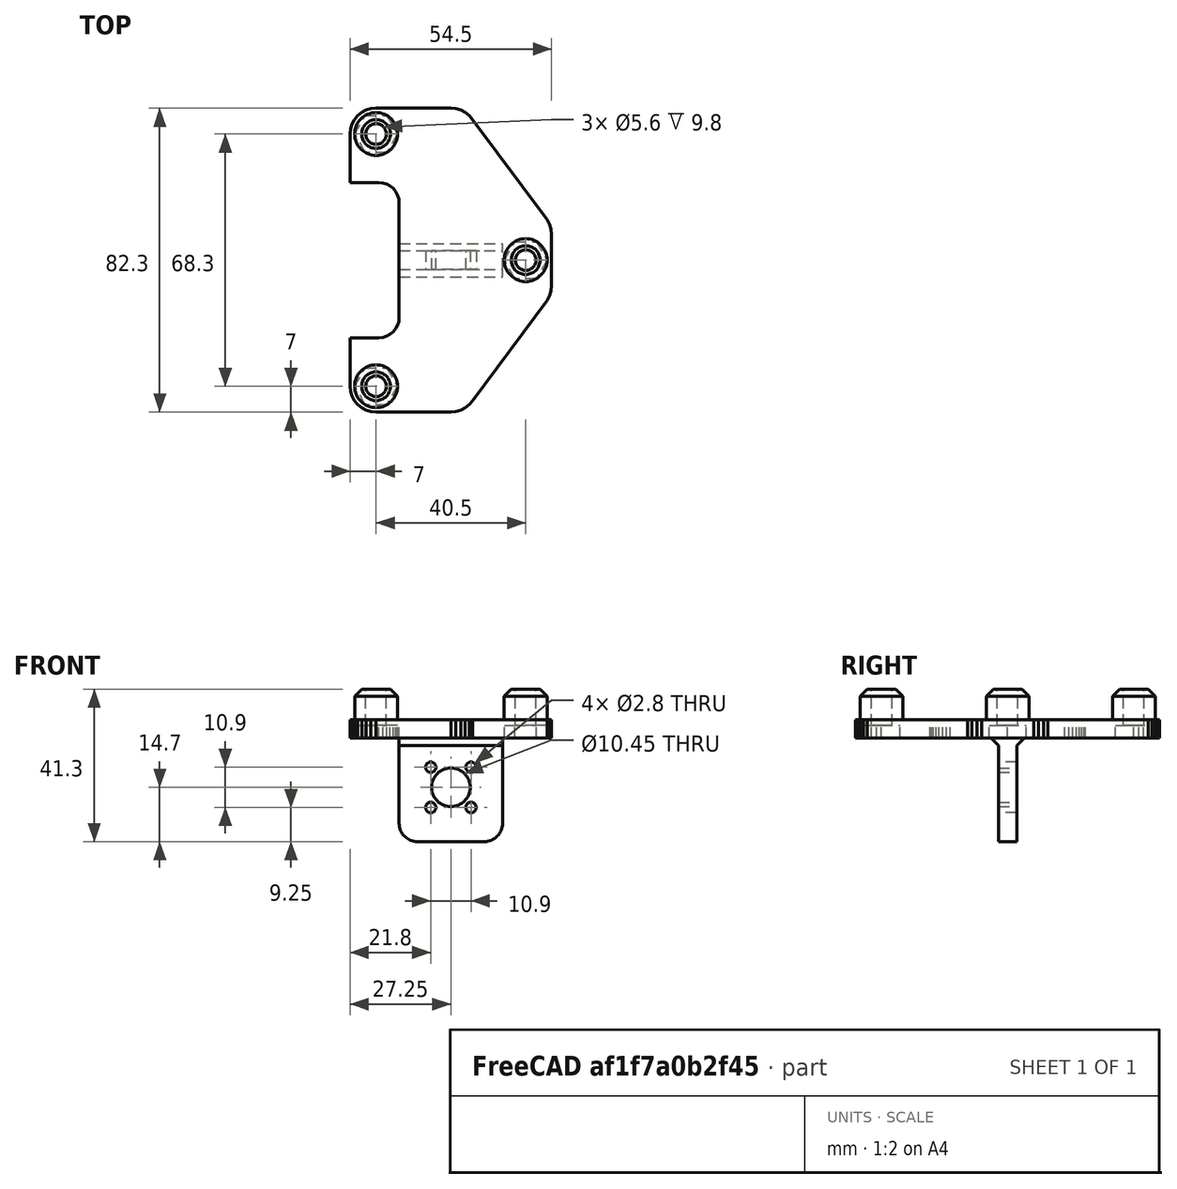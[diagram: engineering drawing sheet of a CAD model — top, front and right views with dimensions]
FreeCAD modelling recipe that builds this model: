
FCSTD DOCUMENT  (FreeCAD 0.19R24267 +99 (Git))
Label: carroZ_1
License: All rights reserved
LicenseURL: http://en.wikipedia.org/wiki/All_rights_reserved
objects: Part::Feature×75, Part::Part2DObjectPython×10, Part::Cylinder×6, Part::Cut×5, Part::FeaturePython×4, Part::MultiFuse×4, Part::Prism×4, Part::Chamfer×3, Part::Extrusion×2, Part::Fuse×2, Part::Plane×1, Part::Box×1, App::DocumentObjectGroupPython×1, Part::Refine×1, Part::Fillet×1
note: 119 computed .brp shape members not serialized (recipe doc carries the construction recipe); baked Part::Feature solids carry a one-line shape summary decoded from their .brp

FEATURE [Part::Feature] polygon
  shape: bbox 40.5 x 68.3 x 2e-07 mm, 1 faces, 0 solids (baked)
FEATURE [Part::Part2DObjectPython] circle  # Draft 2D object (typed FeaturePython)
  Area = 153.938
  FirstAngle = 0
  LastAngle = 0
  MakeFace = true
  Radius = 7
FEATURE [Part::FeaturePython] minkowski  # WARN: FeaturePython — macro-defined, semantics opaque (R4)
  Arguments = {'convexity': '0'}
  Children = -> [polygon,circle]
  Operation = minkowski
FEATURE [Part::Part2DObjectPython] circle001  # Draft 2D object (typed FeaturePython)
  Area = 24.6301
  FirstAngle = 0
  LastAngle = 0
  MakeFace = true
  Placement = pos=(-20.25,-34.15,0) rot=(0,0,1;0rad)
  Radius = 2.8
FEATURE [Part::Part2DObjectPython] circle002  # Draft 2D object (typed FeaturePython)
  Area = 24.6301
  FirstAngle = 0
  LastAngle = 0
  MakeFace = true
  Placement = pos=(-20.25,34.15,0) rot=(0,0,1;0rad)
  Radius = 2.8
FEATURE [Part::Part2DObjectPython] circle003  # Draft 2D object (typed FeaturePython)
  Area = 24.6301
  FirstAngle = 0
  LastAngle = 0
  MakeFace = true
  Placement = pos=(20.25,0,0) rot=(0,0,1;0rad)
  Radius = 2.8
FEATURE [Part::Plane] square
  AttacherType = Attacher::AttachEngine3D
  Length = 31
  Placement = pos=(-15.5,-15.5,0) rot=(0,0,1;0rad)
  Width = 31
FEATURE [Part::Part2DObjectPython] circle004  # Draft 2D object (typed FeaturePython)
  Area = 95.0332
  FirstAngle = 0
  LastAngle = 0
  MakeFace = true
  Radius = 5.5
FEATURE [Part::FeaturePython] minkowski001  # WARN: FeaturePython — macro-defined, semantics opaque (R4)
  Arguments = {'convexity': '0'}
  Children = -> [square,circle004]
  Operation = minkowski
  Placement = pos=(-35,0,0) rot=(0,0,1;0rad)
FEATURE [Part::MultiFuse] union
  Shapes = -> [circle001,circle002,circle003,minkowski001]
FEATURE [Part::Cut] difference
  Base = -> minkowski
  Tool = -> union
FEATURE [Part::FeaturePython] RefineLinearExtrude  # WARN: FeaturePython — macro-defined, semantics opaque (R4)
  Base = -> difference
FEATURE [Part::Extrusion] LinearExtrude
  Base = -> RefineLinearExtrude
  Dir = (0,0,5)
  DirMode = 0
  FaceMakerClass = Part::FaceMakerBullseye
  LengthFwd = 0
  LengthRev = 0
  Solid = false
  Symmetric = false
FEATURE [Part::Cylinder] cylinder
  Angle = 360
  AttacherType = Attacher::AttachEngine3D
  Height = 13.3
  Radius = 5.8
FEATURE [Part::Cylinder] cylinder001
  Angle = 360
  AttacherType = Attacher::AttachEngine3D
  Height = 53.2
  Placement = pos=(0,0,-26.6) rot=(0,0,1;0rad)
  Radius = 2.8
FEATURE [Part::Cut] difference001
  Base = -> cylinder
  Placement = pos=(-20.25,-34.15,0) rot=(0,0,1;0rad)
  Tool = -> cylinder001
FEATURE [Part::Cylinder] cylinder002
  Angle = 360
  AttacherType = Attacher::AttachEngine3D
  Height = 13.3
  Radius = 5.8
FEATURE [Part::Cylinder] cylinder003
  Angle = 360
  AttacherType = Attacher::AttachEngine3D
  Height = 53.2
  Placement = pos=(0,0,-26.6) rot=(0,0,1;0rad)
  Radius = 2.8
FEATURE [Part::Cut] difference002
  Base = -> cylinder002
  Placement = pos=(-20.25,34.15,0) rot=(0,0,1;0rad)
  Tool = -> cylinder003
FEATURE [Part::Cylinder] cylinder004
  Angle = 360
  AttacherType = Attacher::AttachEngine3D
  Height = 13.3
  Radius = 5.8
FEATURE [Part::Cylinder] cylinder005
  Angle = 360
  AttacherType = Attacher::AttachEngine3D
  Height = 53.2
  Placement = pos=(0,0,-26.6) rot=(0,0,1;0rad)
  Radius = 2.8
FEATURE [Part::Cut] difference003
  Base = -> cylinder004
  Placement = pos=(20.25,0,0) rot=(0,0,1;0rad)
  Tool = -> cylinder005
FEATURE [Part::Box] cube
  AttacherType = Attacher::AttachEngine3D
  Height = 28
  Length = 28
  Placement = pos=(-14,-2.5,-28) rot=(0,0,1;0rad)
  Width = 5
FEATURE [Part::MultiFuse] union001
  Shapes = -> [LinearExtrude,difference001,difference002,difference003,cube]
FEATURE [Part::Prism] prism
  AttacherType = Attacher::AttachEngine3D
  Circumradius = 5.79
  FirstAngle = 0
  Height = 7
  Placement = pos=(-20.25,-34.15,-3.5) rot=(0,0,1;0rad)
  Polygon = 6
  SecondAngle = 0
FEATURE [Part::Prism] prism001
  AttacherType = Attacher::AttachEngine3D
  Circumradius = 5.79
  FirstAngle = 0
  Height = 7
  Placement = pos=(-20.25,34.15,-3.5) rot=(0,0,1;0rad)
  Polygon = 6
  SecondAngle = 0
FEATURE [Part::Prism] prism002
  AttacherType = Attacher::AttachEngine3D
  Circumradius = 5.79
  FirstAngle = 0
  Height = 7
  Placement = pos=(20.25,0,-3.5) rot=(0,0,1;0rad)
  Polygon = 6
  SecondAngle = 0
FEATURE [Part::Prism] prism003
  AttacherType = Attacher::AttachEngine3D
  Circumradius = 5.79
  FirstAngle = 0
  Height = 57
  Placement = pos=(20.25,0,-53.5) rot=(0,0,1;0rad)
  Polygon = 6
  SecondAngle = 0
FEATURE [Part::MultiFuse] Group
  Shapes = -> [prism,prism001,prism002,prism003]
FEATURE [Part::Part2DObjectPython] circle005  # Draft 2D object (typed FeaturePython)
  Area = 85.7674
  FirstAngle = 0
  LastAngle = 0
  MakeFace = true
  Radius = 5.225
FEATURE [Part::Part2DObjectPython] circle006  # Draft 2D object (typed FeaturePython)
  Area = 6.15752
  FirstAngle = 0
  LastAngle = 0
  MakeFace = true
  Placement = pos=(5.45,5.45,0) rot=(0,0,1;0rad)
  Radius = 1.4
FEATURE [Part::Part2DObjectPython] circle007  # Draft 2D object (typed FeaturePython)
  Area = 6.15752
  FirstAngle = 0
  LastAngle = 0
  MakeFace = true
  Placement = pos=(-5.45,5.45,0) rot=(0,0,1;1.5708rad)
  Radius = 1.4
FEATURE [Part::Part2DObjectPython] circle008  # Draft 2D object (typed FeaturePython)
  Area = 6.15752
  FirstAngle = 0
  LastAngle = 0
  MakeFace = true
  Placement = pos=(-5.45,-5.45,0) rot=(0,0,1;3.14159rad)
  Radius = 1.4
FEATURE [Part::Part2DObjectPython] circle009  # Draft 2D object (typed FeaturePython)
  Area = 6.15752
  FirstAngle = 0
  LastAngle = 0
  MakeFace = true
  Placement = pos=(5.45,-5.45,0) rot=(0,0,-1;1.5708rad)
  Radius = 1.4
FEATURE [Part::MultiFuse] Group001
  Shapes = -> [circle006,circle007,circle008,circle009]
FEATURE [Part::Fuse] Group002
  Base = -> circle005
  Tool = -> Group001
FEATURE [Part::FeaturePython] RefineLinearExtrude001  # WARN: FeaturePython — macro-defined, semantics opaque (R4)
  Base = -> Group002
FEATURE [Part::Extrusion] LinearExtrude001
  Base = -> RefineLinearExtrude001
  Dir = (0,0,100)
  DirMode = 0
  FaceMakerClass = Part::FaceMakerBullseye
  LengthFwd = 0
  LengthRev = 0
  Placement = pos=(0,50,-13.3) rot=(1,0,0;1.5708rad)
  Solid = false
  Symmetric = false
FEATURE [Part::Fuse] union002
  Base = -> Group
  Tool = -> LinearExtrude001
FEATURE [Part::Cut] difference004
  Base = -> union001
  Tool = -> union002
FEATURE [App::DocumentObjectGroupPython] LayerContainer  label="Capas"  # scripted group (container) (typed FeaturePython)
FEATURE [Part::Feature] Line
  shape: bbox 1.313 x 0.3984 x 2e-07 mm, 0 faces, 0 solids (baked)
FEATURE [Part::Feature] Line001
  shape: bbox 1.365 x 0.1348 x 2e-07 mm, 0 faces, 0 solids (baked)
FEATURE [Part::Feature] Line002
  shape: bbox 20.25 x 2e-07 x 2e-07 mm, 0 faces, 0 solids (baked)
FEATURE [Part::Feature] Line003
  shape: bbox 1.365 x 0.1348 x 2e-07 mm, 0 faces, 0 solids (baked)
FEATURE [Part::Feature] Line004
  shape: bbox 1.314 x 0.3984 x 2e-07 mm, 0 faces, 0 solids (baked)
FEATURE [Part::Feature] Line005
  shape: bbox 1.21 x 0.6465 x 2e-07 mm, 0 faces, 0 solids (baked)
FEATURE [Part::Feature] Line006
  shape: bbox 1.062 x 0.8701 x 2e-07 mm, 0 faces, 0 solids (baked)
FEATURE [Part::Feature] Line007
  shape: bbox 0.8701 x 1.062 x 2e-07 mm, 0 faces, 0 solids (baked)
FEATURE [Part::Feature] Line008
  shape: bbox 0.6465 x 1.21 x 2e-07 mm, 0 faces, 0 solids (baked)
FEATURE [Part::Feature] Line009
  shape: bbox 0.3984 x 1.314 x 2e-07 mm, 0 faces, 0 solids (baked)
FEATURE [Part::Feature] Line010
  shape: bbox 0.1348 x 1.365 x 2e-07 mm, 0 faces, 0 solids (baked)
FEATURE [Part::Feature] Line011
  shape: bbox 2e-07 x 68.3 x 2e-07 mm, 0 faces, 0 solids (baked)
FEATURE [Part::Feature] Line012
  shape: bbox 0.1348 x 1.365 x 2e-07 mm, 0 faces, 0 solids (baked)
FEATURE [Part::Feature] Line013
  shape: bbox 0.3984 x 1.314 x 2e-07 mm, 0 faces, 0 solids (baked)
FEATURE [Part::Feature] Line014
  shape: bbox 0.6465 x 1.21 x 2e-07 mm, 0 faces, 0 solids (baked)
FEATURE [Part::Feature] Line015
  shape: bbox 0.8701 x 1.062 x 2e-07 mm, 0 faces, 0 solids (baked)
FEATURE [Part::Feature] Line016
  shape: bbox 1.062 x 0.8701 x 2e-07 mm, 0 faces, 0 solids (baked)
FEATURE [Part::Feature] Line017
  shape: bbox 1.21 x 0.6465 x 2e-07 mm, 0 faces, 0 solids (baked)
FEATURE [Part::Feature] Line018
  shape: bbox 1.314 x 0.3984 x 2e-07 mm, 0 faces, 0 solids (baked)
FEATURE [Part::Feature] Line019
  shape: bbox 1.365 x 0.1348 x 2e-07 mm, 0 faces, 0 solids (baked)
FEATURE [Part::Feature] Line020
  shape: bbox 20.25 x 2e-07 x 2e-07 mm, 0 faces, 0 solids (baked)
FEATURE [Part::Feature] Line021
  shape: bbox 1.365 x 0.1348 x 2e-07 mm, 0 faces, 0 solids (baked)
FEATURE [Part::Feature] Line022
  shape: bbox 1.313 x 0.3984 x 2e-07 mm, 0 faces, 0 solids (baked)
FEATURE [Part::Feature] Line023
  shape: bbox 1.21 x 0.6465 x 2e-07 mm, 0 faces, 0 solids (baked)
FEATURE [Part::Feature] Line024
  shape: bbox 1.062 x 0.8701 x 2e-07 mm, 0 faces, 0 solids (baked)
FEATURE [Part::Feature] Line025
  shape: bbox 0.8701 x 1.062 x 2e-07 mm, 0 faces, 0 solids (baked)
FEATURE [Part::Feature] Line026
  shape: bbox 20.25 x 27.15 x 2e-07 mm, 0 faces, 0 solids (baked)
FEATURE [Part::Feature] Line027
  shape: bbox 0.6465 x 1.21 x 2e-07 mm, 0 faces, 0 solids (baked)
FEATURE [Part::Feature] Line028
  shape: bbox 0.3984 x 1.313 x 2e-07 mm, 0 faces, 0 solids (baked)
FEATURE [Part::Feature] Line029
  shape: bbox 0.1348 x 1.365 x 2e-07 mm, 0 faces, 0 solids (baked)
FEATURE [Part::Feature] Line030
  shape: bbox 2e-07 x 14 x 2e-07 mm, 0 faces, 0 solids (baked)
FEATURE [Part::Feature] Line031
  shape: bbox 0.1348 x 1.365 x 2e-07 mm, 0 faces, 0 solids (baked)
FEATURE [Part::Feature] Line032
  shape: bbox 0.3984 x 1.313 x 2e-07 mm, 0 faces, 0 solids (baked)
FEATURE [Part::Feature] Line033
  shape: bbox 0.6465 x 1.21 x 2e-07 mm, 0 faces, 0 solids (baked)
FEATURE [Part::Feature] Line034
  shape: bbox 20.25 x 27.15 x 2e-07 mm, 0 faces, 0 solids (baked)
FEATURE [Part::Feature] Line035
  shape: bbox 0.8701 x 1.062 x 2e-07 mm, 0 faces, 0 solids (baked)
FEATURE [Part::Feature] Line036
  shape: bbox 1.062 x 0.8701 x 2e-07 mm, 0 faces, 0 solids (baked)
FEATURE [Part::Feature] Line037
  shape: bbox 1.21 x 0.6465 x 2e-07 mm, 0 faces, 0 solids (baked)
FEATURE [Part::Feature] Line038
  shape: bbox 0.833 x 0.6845 x 2e-07 mm, 0 faces, 0 solids (baked)
FEATURE [Part::Feature] Line039
  shape: bbox 0.6845 x 0.833 x 2e-07 mm, 0 faces, 0 solids (baked)
FEATURE [Part::Feature] Line040
  shape: bbox 0.5079 x 0.9512 x 2e-07 mm, 0 faces, 0 solids (baked)
FEATURE [Part::Feature] Line041
  shape: bbox 0.3134 x 1.031 x 2e-07 mm, 0 faces, 0 solids (baked)
FEATURE [Part::Feature] Line042
  shape: bbox 0.1055 x 1.073 x 2e-07 mm, 0 faces, 0 solids (baked)
FEATURE [Part::Feature] Line043
  shape: bbox 2e-07 x 31 x 2e-07 mm, 0 faces, 0 solids (baked)
FEATURE [Part::Feature] Line044
  shape: bbox 0.1055 x 1.073 x 2e-07 mm, 0 faces, 0 solids (baked)
FEATURE [Part::Feature] Line045
  shape: bbox 0.3134 x 1.031 x 2e-07 mm, 0 faces, 0 solids (baked)
FEATURE [Part::Feature] Line046
  shape: bbox 0.5079 x 0.9512 x 2e-07 mm, 0 faces, 0 solids (baked)
FEATURE [Part::Feature] Line047
  shape: bbox 0.6845 x 0.833 x 2e-07 mm, 0 faces, 0 solids (baked)
FEATURE [Part::Feature] Line048
  shape: bbox 0.833 x 0.6845 x 2e-07 mm, 0 faces, 0 solids (baked)
FEATURE [Part::Feature] Line049
  shape: bbox 0.9512 x 0.5079 x 2e-07 mm, 0 faces, 0 solids (baked)
FEATURE [Part::Feature] Line050
  shape: bbox 1.031 x 0.3134 x 2e-07 mm, 0 faces, 0 solids (baked)
FEATURE [Part::Feature] Line051
  shape: bbox 1.073 x 0.1055 x 2e-07 mm, 0 faces, 0 solids (baked)
FEATURE [Part::Feature] Line052
  shape: bbox 31 x 2e-07 x 2e-07 mm, 0 faces, 0 solids (baked)
FEATURE [Part::Feature] Line053
  shape: bbox 1.073 x 0.1055 x 2e-07 mm, 0 faces, 0 solids (baked)
FEATURE [Part::Feature] Line054
  shape: bbox 1.031 x 0.3134 x 2e-07 mm, 0 faces, 0 solids (baked)
FEATURE [Part::Feature] Line055
  shape: bbox 0.9512 x 0.5079 x 2e-07 mm, 0 faces, 0 solids (baked)
FEATURE [Part::Feature] Line056
  shape: bbox 0.833 x 0.6845 x 2e-07 mm, 0 faces, 0 solids (baked)
FEATURE [Part::Feature] Line057
  shape: bbox 0.6845 x 0.833 x 2e-07 mm, 0 faces, 0 solids (baked)
FEATURE [Part::Feature] Line058
  shape: bbox 0.5079 x 0.9512 x 2e-07 mm, 0 faces, 0 solids (baked)
FEATURE [Part::Feature] Line059
  shape: bbox 0.3134 x 1.031 x 2e-07 mm, 0 faces, 0 solids (baked)
FEATURE [Part::Feature] Line060
  shape: bbox 0.1055 x 1.073 x 2e-07 mm, 0 faces, 0 solids (baked)
FEATURE [Part::Feature] Line061
  shape: bbox 2e-07 x 31 x 2e-07 mm, 0 faces, 0 solids (baked)
FEATURE [Part::Feature] Line062
  shape: bbox 0.1055 x 1.073 x 2e-07 mm, 0 faces, 0 solids (baked)
FEATURE [Part::Feature] Line063
  shape: bbox 0.3134 x 1.031 x 2e-07 mm, 0 faces, 0 solids (baked)
FEATURE [Part::Feature] Line064
  shape: bbox 0.5079 x 0.9512 x 2e-07 mm, 0 faces, 0 solids (baked)
FEATURE [Part::Feature] Line065
  shape: bbox 0.6845 x 0.833 x 2e-07 mm, 0 faces, 0 solids (baked)
FEATURE [Part::Feature] Line066
  shape: bbox 0.833 x 0.6845 x 2e-07 mm, 0 faces, 0 solids (baked)
FEATURE [Part::Feature] Line067
  shape: bbox 0.9512 x 0.5079 x 2e-07 mm, 0 faces, 0 solids (baked)
FEATURE [Part::Feature] Line068
  shape: bbox 1.031 x 0.3134 x 2e-07 mm, 0 faces, 0 solids (baked)
FEATURE [Part::Feature] Line069
  shape: bbox 1.073 x 0.1055 x 2e-07 mm, 0 faces, 0 solids (baked)
FEATURE [Part::Feature] Line070
  shape: bbox 31 x 2e-07 x 2e-07 mm, 0 faces, 0 solids (baked)
FEATURE [Part::Feature] Line071
  shape: bbox 1.073 x 0.1055 x 2e-07 mm, 0 faces, 0 solids (baked)
FEATURE [Part::Feature] Line072
  shape: bbox 1.031 x 0.3134 x 2e-07 mm, 0 faces, 0 solids (baked)
FEATURE [Part::Feature] Line073
  shape: bbox 0.9512 x 0.5079 x 2e-07 mm, 0 faces, 0 solids (baked)
FEATURE [Part::Refine] difference004001
  Source = -> difference004
FEATURE [Part::Chamfer] Chamfer
  Base = -> difference004001
  Edges = 3 edges r=1.9: [Edge178,Edge180,Edge182]
FEATURE [Part::Fillet] Fillet
  Base = -> Chamfer
  Edges = 2 edges r=5: [Edge159,Edge221]
FEATURE [Part::Chamfer] Chamfer001
  Base = -> Fillet
  Edges = 1 edges r=2: [Edge11]
FEATURE [Part::Chamfer] Chamfer002
  Base = -> Chamfer001
  Edges = 1 edges r=2: [Edge26]
